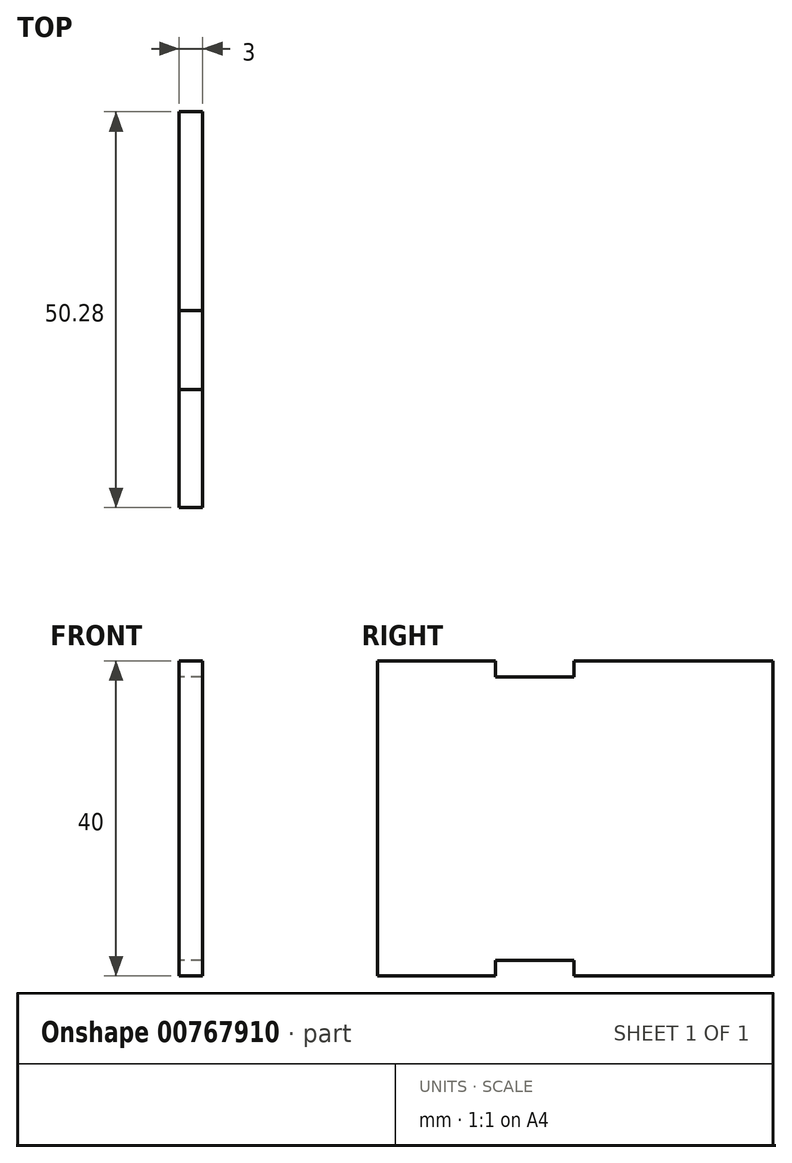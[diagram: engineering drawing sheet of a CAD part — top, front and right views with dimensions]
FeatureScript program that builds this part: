
annotation { "Feature Type Name" : "Feature", "Feature Type Description" : "" }
export const myFeature = defineFeature(function(context is Context, id is Id, definition is map)
    precondition{}
    {
        {
            var Q0;
            Q0=qCreatedBy(makeId("Right.planeOp"),FACE);
            var sketch = newSketch(context, id + "F0", { "sketchPlane" : qUnion([Q0])});
            skLineSegment(sketch, "E0.bottom", {"start": v(0, 0) * mm, "end": v(15, 0) * mm});
            skLineSegment(sketch, "E0.top", {"start": v(0, 40) * mm, "end": v(15, 40) * mm});
            skLineSegment(sketch, "E0.left", {"start": v(0, 0) * mm, "end": v(0, 40) * mm});
            skLineSegment(sketch, "E0.right", {"start": v(50.28, 0) * mm, "end": v(50.28, 40) * mm});
            skLineSegment(sketch, "E1.0", {"start": v(15, 0) * mm, "end": v(15, 2) * mm});
            skLineSegment(sketch, "E2.0", {"start": v(25, 0) * mm, "end": v(25, 2) * mm});
            skLineSegment(sketch, "E3", {"start": v(15, 38) * mm, "end": v(25, 38) * mm});
            skLineSegment(sketch, "E4", {"start": v(15, 2) * mm, "end": v(25, 2) * mm});
            skLineSegment(sketch, "E5.trimOffspring", {"start": v(25, 40) * mm, "end": v(50.28, 40) * mm});
            skLineSegment(sketch, "E6.trimOffspring", {"start": v(25, 0) * mm, "end": v(50.28, 0) * mm});
            skLineSegment(sketch, "E7.trimOffspring", {"start": v(15, 38) * mm, "end": v(15, 40) * mm});
            skLineSegment(sketch, "E8.trimOffspring", {"start": v(25, 38) * mm, "end": v(25, 40) * mm});
            skSolve(sketch);
        }
        {
            var Q0;
            Q0=makeQuery(id+"F0.imprint","IMPRINT",FACE,{"disambiguationData":[TD([[makeQuery(id+"F0.imprint","IMPRINT",EDGE,{"derivedFrom":sQuery(id+"F0.wireOp",EDGE,"E0.bottom")}),1.0]])]});
            extrude(context, id + "F1", {"entities" : qUnion([Q0]), "depth" : 3 * mm, "offsetDistance" : 25 * mm});
        }
    });
